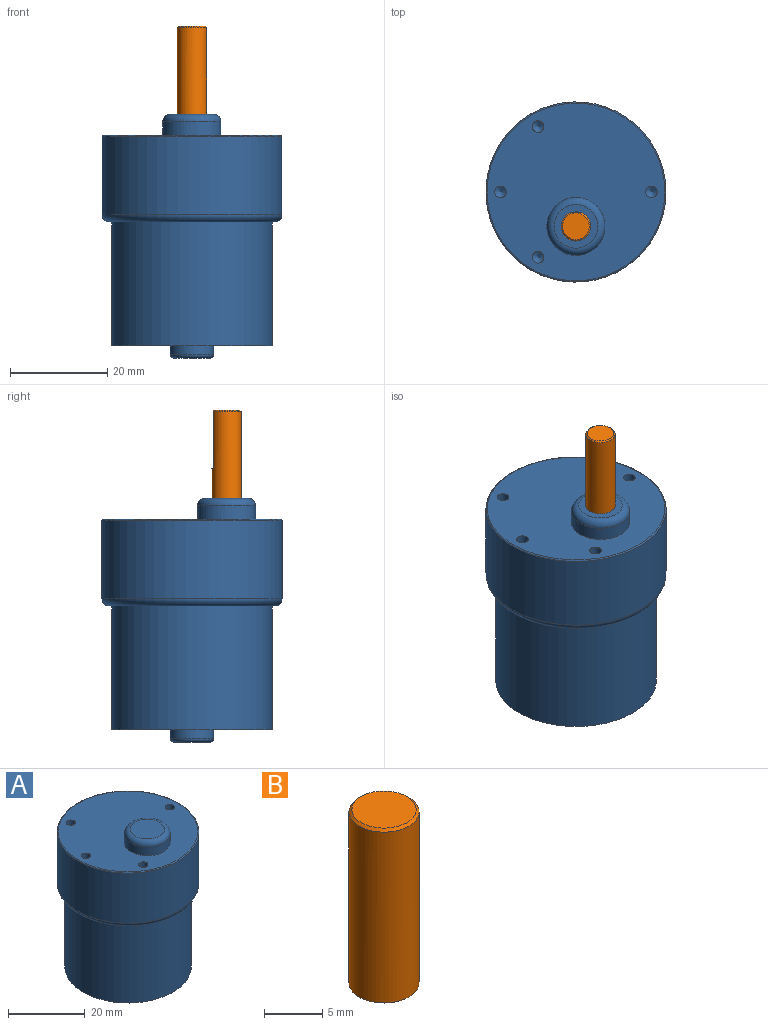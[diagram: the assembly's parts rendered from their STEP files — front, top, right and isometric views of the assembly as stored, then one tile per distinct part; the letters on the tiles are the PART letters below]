
ASSEMBLY  parts=2 mates=1
PART A: 21 faces, bbox 40x40x50 mm
  f0: cylinder r=18.5mm len=37mm, axis (0,0,-1), area 1863.3mm2, adj f10,f12
  f1: plane 36.5x36.5mm, normal (0,0,1), area 916.3mm2, adj f3,f12,f13,f15,f17,f19
  f2: plane 34x34mm, normal (0,0,-1), area 51.6mm2, adj f5,f10
  f3: cylinder r=5.97mm len=11.94mm, axis (0,0,-1), area 105.7mm2, adj f1,f11
  f4: plane 8.94x8.94mm, normal (0,0,1), area 62.7mm2, adj f11
  f5: cylinder r=16.51mm len=33.02mm, axis (0,0,1), area 2634.9mm2, adj f2,f6
  f6: plane 33.02x33.02mm, normal (0,0,-1), area 794.3mm2, adj f5,f7
  f7: cylinder r=4.45mm len=8.89mm, axis (0,0,1), area 53.2mm2, adj f6,f9
  f8: plane 7.62x7.62mm, normal (0,0,-1), area 45.6mm2, adj f9
  f9: torus R=3.81mm, axis (0,0,-1), area 26.4mm2, adj f7,f8
  f10: torus R=17mm, axis (0,0,1), area 265.8mm2, adj f0,f2
  f11: torus R=4.47mm, axis (0,0,1), area 80.3mm2, adj f3,f4
  f12: torus R=18.25mm, axis (0,0,1), area 45.4mm2, adj f0,f1
  f13: cylinder r=1.2mm len=5mm, axis (0,0,1), area 37.7mm2, adj f1,f14
  f14: cone r=0mm half-angle=59deg, axis (0,0,1), area 5.3mm2, adj f13
  f15: cylinder r=1.2mm len=5mm, axis (0,0,1), area 37.7mm2, adj f1,f16
  f16: cone r=0mm half-angle=59deg, axis (0,0,1), area 5.3mm2, adj f15
  f17: cylinder r=1.2mm len=5mm, axis (0,0,1), area 37.7mm2, adj f1,f18
  f18: cone r=0mm half-angle=59deg, axis (0,0,1), area 5.3mm2, adj f17
  f19: cylinder r=1.2mm len=5mm, axis (0,0,1), area 37.7mm2, adj f1,f20
  f20: cone r=0mm half-angle=59deg, axis (0,0,1), area 5.3mm2, adj f19
PART B: 6 faces, bbox 6x6x18.2 mm
  f0: cylinder r=3mm len=17.91mm, axis (0,0,-1), area 308.8mm2, adj f2,f3,f4,f5
  f1: plane 5.5x5.5mm, normal (0,0,1), area 23.8mm2, adj f5
  f2: plane 6x6mm, normal (0,0,-1), area 28.3mm2, adj f0
  f3: plane 12x2.39mm, normal (0,1,0), area 28.4mm2, adj f0,f4,f5
  f4: plane 2.38x0.25mm, normal (0,0,1), area 0.4mm2, adj f0,f3
  f5: cone r=2.75mm half-angle=45deg, axis (0,0,-1), area 5.8mm2, adj f0,f1,f3
PLACE A at identity
PLACE B at identity
MATE revolute B.f0 <-> A.f3  axis (0,0,-1) through (0,-7.1,22.1)mm
